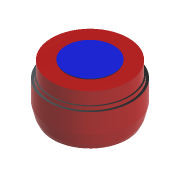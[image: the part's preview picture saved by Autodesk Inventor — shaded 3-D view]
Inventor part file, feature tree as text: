
AUTODESK INVENTOR PART (.ipt)
format: ipt  version: 2021 (Build 250183000, 183)  size: 178,688 bytes
history: native  units: mm
features: sketch x5, extrude x4, revolve x1, other x1
ambient origin geometry x8: Origin, YZ Plane, XZ Plane, XY Plane, X Axis, Y Axis, Z Axis, Center Point
bodies: Solid1 (feature_tree), Solid2 (feature_tree), Solid3 (feature_tree)
feature tree (11):
  revolve  "Revolution1"  [1 undecoded]
  extrude  "Extrusion1"  Depth=4.0mm
  extrude  "Extrusion: Lens Imitation"  Depth=72.0mm
  extrude  "Extrusion: Lens imitation 1"  Depth=17.0mm
  extrude  "Extrusion5"  Depth=1.0mm
  sketch  "Sketch1"  dims[d2=58.0mm d3=0.84mm]
  sketch  "Sketch4"  dims[d5=64.0mm d6=4.0mm]
  sketch  "Sketch6"  dims[d7=67.7mm d8=72.0mm]
  sketch  "Sketch7"  dims[d9=9.0mm d10=17.0mm]
  sketch  "Sketch8"  dims[d11=3.0mm d12=68.3mm d13=10.5mm d14=66.0mm d18=90.0deg d19=36.0mm d20=10.0mm d21=0.0mm d24=1.0mm d25=0.0mm d26=1.0mm d27=0.0mm d28=22.0mm d29=1.0mm d30=1.0mm d31=0.0mm]
  other  "LightSheet"
note: 1 required parameter value undecoded (feature->parameter linkage not recoverable at this tier; creation-order binding heuristic only, values carry confidence <= 0.55)
